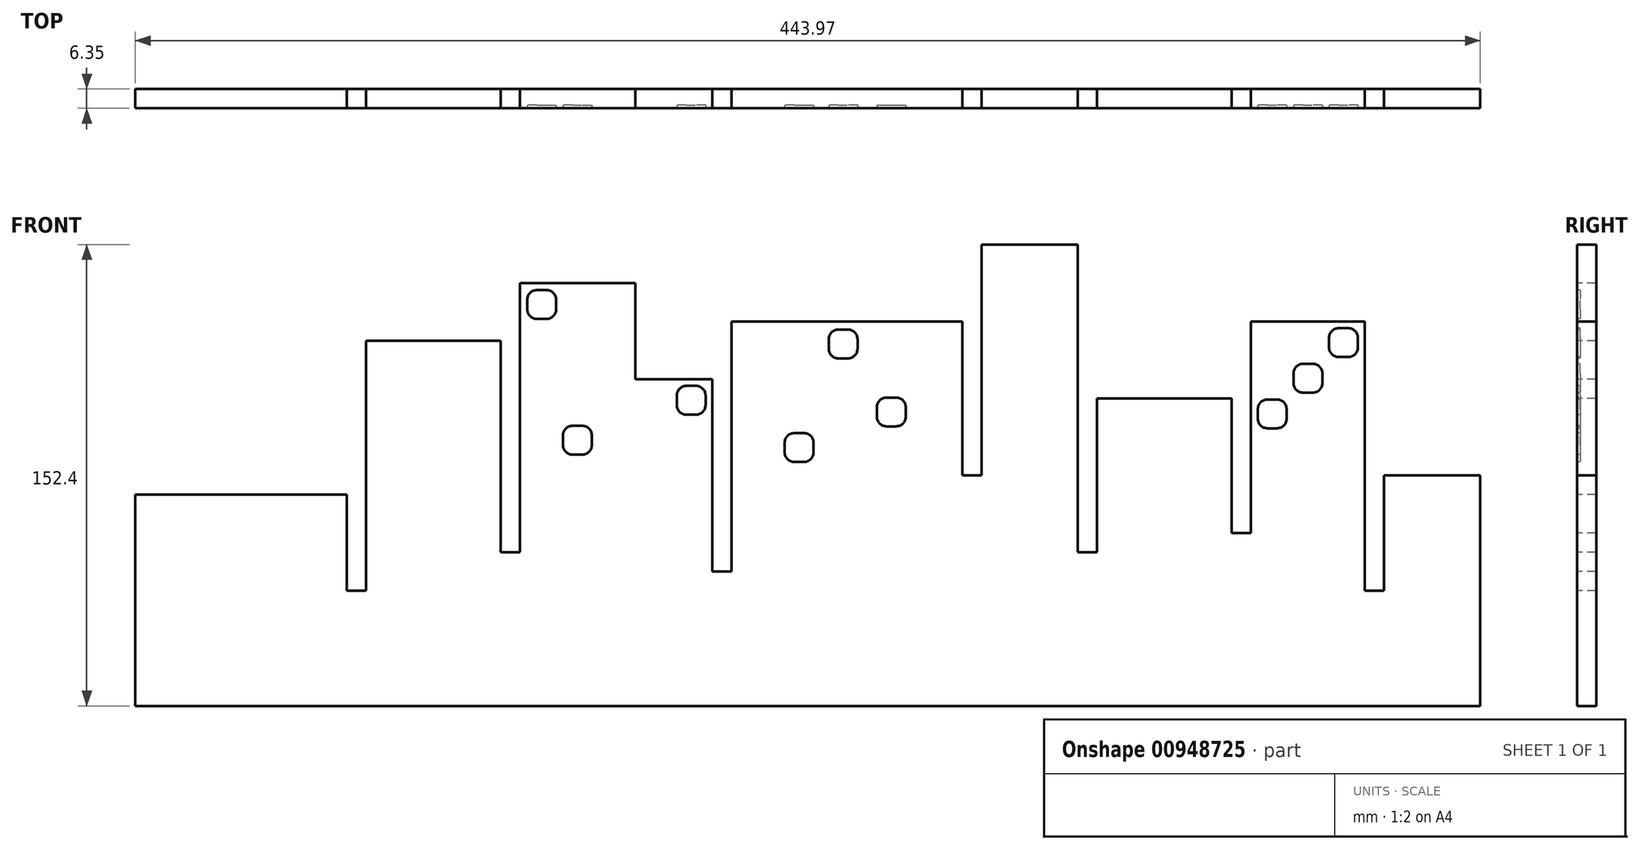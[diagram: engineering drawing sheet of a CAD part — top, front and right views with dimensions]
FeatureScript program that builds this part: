
annotation { "Feature Type Name" : "Feature", "Feature Type Description" : "" }
export const myFeature = defineFeature(function(context is Context, id is Id, definition is map)
    precondition{}
    {
        {
            var Q0;
            Q0=qCreatedBy(makeId("Front.planeOp"),FACE);
            var sketch = newSketch(context, id + "F0", { "sketchPlane" : qUnion([Q0])});
            skLineSegment(sketch, "E0.bottom", {"start": v(-28.68, 31.43) * mm, "end": v(-25.5, 31.43) * mm});
            skLineSegment(sketch, "E0.top", {"start": v(-28.68, 21.9) * mm, "end": v(-25.5, 21.9) * mm});
            skLineSegment(sketch, "E0.left", {"start": v(-31.86, 28.26) * mm, "end": v(-31.86, 25.08) * mm});
            skLineSegment(sketch, "E0.right", {"start": v(-22.33, 28.26) * mm, "end": v(-22.33, 25.08) * mm});
            skPoint(sketch, "E1.visualSharp", {"position": v(-31.86, 31.43) * mm});
            skArc(sketch, "E1.filletArc", {"start": v(-28.68, 31.43) * mm, "mid": v(-30.93, 30.5) * mm, "end": v(-31.86, 28.26) * mm});
            skPoint(sketch, "E2.visualSharp", {"position": v(-22.33, 31.43) * mm});
            skArc(sketch, "E2.filletArc", {"start": v(-22.33, 28.26) * mm, "mid": v(-23.26, 30.5) * mm, "end": v(-25.5, 31.43) * mm});
            skPoint(sketch, "E3.visualSharp", {"position": v(-22.33, 21.9) * mm});
            skArc(sketch, "E3.filletArc", {"start": v(-25.5, 21.9) * mm, "mid": v(-23.26, 22.84) * mm, "end": v(-22.33, 25.08) * mm});
            skPoint(sketch, "E4.visualSharp", {"position": v(-31.86, 21.9) * mm});
            skArc(sketch, "E4.filletArc", {"start": v(-31.86, 25.08) * mm, "mid": v(-30.93, 22.84) * mm, "end": v(-28.68, 21.9) * mm});
            skLineSegment(sketch, "E5", {"start": v(-22.33, 31.43) * mm, "end": v(-20.09, 33.68) * mm});
            skLineSegment(sketch, "E6.bottom", {"start": v(-16.91, 43.2) * mm, "end": v(-13.74, 43.2) * mm});
            skLineSegment(sketch, "E6.top", {"start": v(-16.91, 33.68) * mm, "end": v(-13.74, 33.68) * mm});
            skLineSegment(sketch, "E6.left", {"start": v(-20.09, 40.03) * mm, "end": v(-20.09, 36.85) * mm});
            skLineSegment(sketch, "E6.right", {"start": v(-10.56, 40.03) * mm, "end": v(-10.56, 36.85) * mm});
            skPoint(sketch, "E7.visualSharp", {"position": v(-20.09, 43.2) * mm});
            skArc(sketch, "E7.filletArc", {"start": v(-16.91, 43.2) * mm, "mid": v(-19.16, 42.27) * mm, "end": v(-20.09, 40.03) * mm});
            skPoint(sketch, "E8.visualSharp", {"position": v(-10.56, 43.2) * mm});
            skArc(sketch, "E8.filletArc", {"start": v(-10.56, 40.03) * mm, "mid": v(-11.5, 42.27) * mm, "end": v(-13.74, 43.2) * mm});
            skPoint(sketch, "E9.visualSharp", {"position": v(-10.56, 33.68) * mm});
            skArc(sketch, "E9.filletArc", {"start": v(-13.74, 33.68) * mm, "mid": v(-11.5, 34.6) * mm, "end": v(-10.56, 36.85) * mm});
            skPoint(sketch, "E10.visualSharp", {"position": v(-20.09, 33.68) * mm});
            skArc(sketch, "E10.filletArc", {"start": v(-20.09, 36.85) * mm, "mid": v(-19.16, 34.6) * mm, "end": v(-16.91, 33.68) * mm});
            skLineSegment(sketch, "E11", {"start": v(-10.56, 43.2) * mm, "end": v(-8.32, 45.45) * mm});
            skLineSegment(sketch, "E12.bottom", {"start": v(-5.14, 54.97) * mm, "end": v(-1.97, 54.97) * mm});
            skLineSegment(sketch, "E12.top", {"start": v(-5.14, 45.45) * mm, "end": v(-1.97, 45.45) * mm});
            skLineSegment(sketch, "E12.left", {"start": v(-8.32, 51.8) * mm, "end": v(-8.32, 48.62) * mm});
            skLineSegment(sketch, "E12.right", {"start": v(1.2, 51.8) * mm, "end": v(1.2, 48.62) * mm});
            skPoint(sketch, "E13.visualSharp", {"position": v(-8.32, 54.97) * mm});
            skArc(sketch, "E13.filletArc", {"start": v(-5.14, 54.97) * mm, "mid": v(-7.39, 54.04) * mm, "end": v(-8.32, 51.8) * mm});
            skPoint(sketch, "E14.visualSharp", {"position": v(1.2, 54.97) * mm});
            skArc(sketch, "E14.filletArc", {"start": v(1.2, 51.8) * mm, "mid": v(0.28, 54.04) * mm, "end": v(-1.97, 54.97) * mm});
            skPoint(sketch, "E15.visualSharp", {"position": v(1.2, 45.45) * mm});
            skArc(sketch, "E15.filletArc", {"start": v(-1.97, 45.45) * mm, "mid": v(0.28, 46.38) * mm, "end": v(1.2, 48.62) * mm});
            skPoint(sketch, "E16.visualSharp", {"position": v(-8.32, 45.45) * mm});
            skArc(sketch, "E16.filletArc", {"start": v(-8.32, 48.62) * mm, "mid": v(-7.39, 46.38) * mm, "end": v(-5.14, 45.45) * mm});
            skPoint(sketch, "E17.visualSharp", {"position": v(-20.9, 30.05) * mm});
            skLineSegment(sketch, "E18", {"start": v(-20.9, 30.05) * mm, "end": v(-18.65, 32.3) * mm});
            skPoint(sketch, "E19.visualSharp", {"position": v(-18.65, 32.3) * mm});
            skPoint(sketch, "E20.visualSharp", {"position": v(-34.1, 19.66) * mm});
            skLineSegment(sketch, "E21", {"start": v(-34.1, 19.66) * mm, "end": v(-31.86, 21.9) * mm});
            skLineSegment(sketch, "E22", {"start": v(1.2, 54.97) * mm, "end": v(3.47, 57.2) * mm});
            skPoint(sketch, "E23.visualSharp", {"position": v(3.47, 57.2) * mm});
            skLineSegment(sketch, "E24.bottom", {"start": v(3.47, 57.2) * mm, "end": v(-34.1, 57.2) * mm});
            skLineSegment(sketch, "E24.left", {"start": v(3.47, 57.2) * mm, "end": v(3.47, -31.7) * mm});
            skLineSegment(sketch, "E24.right", {"start": v(-34.1, 57.2) * mm, "end": v(-34.1, -12.64) * mm});
            skLineSegment(sketch, "E25.right", {"start": v(3.47, 19.66) * mm, "end": v(3.47, 19.65) * mm});
            skLineSegment(sketch, "E26.top", {"start": v(-34.1, -69.8) * mm, "end": v(3.47, -69.8) * mm});
            skLineSegment(sketch, "E27.bottom", {"start": v(9.82, -69.8) * mm, "end": v(41.57, -69.8) * mm});
            skLineSegment(sketch, "E27.top", {"start": v(9.82, 6.4) * mm, "end": v(41.57, 6.4) * mm});
            skLineSegment(sketch, "E27.left", {"start": v(9.82, -31.7) * mm, "end": v(9.82, 6.4) * mm});
            skLineSegment(sketch, "E27.right", {"start": v(41.57, -69.8) * mm, "end": v(41.57, 6.4) * mm});
            skLineSegment(sketch, "E28.bottom", {"start": v(-34.1, -69.8) * mm, "end": v(-40.45, -69.8) * mm});
            skLineSegment(sketch, "E28.top", {"start": v(-34.1, -12.64) * mm, "end": v(-40.45, -12.64) * mm});
            skLineSegment(sketch, "E29.bottom", {"start": v(-40.45, -69.8) * mm, "end": v(-84.9, -69.8) * mm});
            skLineSegment(sketch, "E29.top", {"start": v(-40.45, 31.8) * mm, "end": v(-84.9, 31.8) * mm});
            skLineSegment(sketch, "E29.left", {"start": v(-40.45, -12.64) * mm, "end": v(-40.45, 31.8) * mm});
            skLineSegment(sketch, "E29.right", {"start": v(-84.9, -19) * mm, "end": v(-84.9, 31.8) * mm});
            skLineSegment(sketch, "E30.bottom", {"start": v(-84.9, -69.8) * mm, "end": v(-91.25, -69.8) * mm});
            skLineSegment(sketch, "E30.top", {"start": v(-84.9, -19) * mm, "end": v(-91.25, -19) * mm});
            skLineSegment(sketch, "E31.bottom", {"start": v(-91.25, -69.8) * mm, "end": v(-123, -69.8) * mm});
            skLineSegment(sketch, "E31.top", {"start": v(-91.25, 82.6) * mm, "end": v(-123, 82.6) * mm});
            skLineSegment(sketch, "E31.left", {"start": v(-91.25, -19) * mm, "end": v(-91.25, 82.6) * mm});
            skLineSegment(sketch, "E31.right", {"start": v(-123, 6.4) * mm, "end": v(-123, 82.6) * mm});
            skLineSegment(sketch, "E32.bottom", {"start": v(-123, -69.8) * mm, "end": v(-129.35, -69.8) * mm});
            skLineSegment(sketch, "E32.top", {"start": v(-123, 6.4) * mm, "end": v(-129.35, 6.4) * mm});
            skLineSegment(sketch, "E33.bottom", {"start": v(-129.35, -69.8) * mm, "end": v(-205.55, -69.8) * mm});
            skLineSegment(sketch, "E33.top", {"start": v(-129.35, 57.2) * mm, "end": v(-205.55, 57.2) * mm});
            skLineSegment(sketch, "E33.left", {"start": v(-129.35, 6.4) * mm, "end": v(-129.35, 57.2) * mm});
            skLineSegment(sketch, "E33.right", {"start": v(-205.55, -25.34) * mm, "end": v(-205.55, 57.2) * mm});
            skLineSegment(sketch, "E34.bottom", {"start": v(-205.55, -69.8) * mm, "end": v(-211.9, -69.8) * mm});
            skLineSegment(sketch, "E34.top", {"start": v(-205.55, -25.34) * mm, "end": v(-211.9, -25.34) * mm});
            skLineSegment(sketch, "E35.bottom", {"start": v(-211.9, -69.8) * mm, "end": v(-237.3, -69.8) * mm});
            skLineSegment(sketch, "E35.top", {"start": v(-211.9, 38.16) * mm, "end": v(-237.3, 38.16) * mm});
            skLineSegment(sketch, "E35.left", {"start": v(-211.9, -25.34) * mm, "end": v(-211.9, 38.16) * mm});
            skLineSegment(sketch, "E36.bottom", {"start": v(-237.3, -69.8) * mm, "end": v(-275.4, -69.8) * mm});
            skLineSegment(sketch, "E36.top", {"start": v(-237.3, 69.9) * mm, "end": v(-275.4, 69.9) * mm});
            skLineSegment(sketch, "E36.left", {"start": v(-237.3, 38.16) * mm, "end": v(-237.3, 69.9) * mm});
            skLineSegment(sketch, "E36.right", {"start": v(-275.4, -19) * mm, "end": v(-275.4, 69.9) * mm});
            skLineSegment(sketch, "E37.bottom", {"start": v(-275.4, -69.8) * mm, "end": v(-281.75, -69.8) * mm});
            skLineSegment(sketch, "E37.top", {"start": v(-275.4, -19) * mm, "end": v(-281.75, -19) * mm});
            skLineSegment(sketch, "E38.bottom", {"start": v(-281.75, -69.8) * mm, "end": v(-326.2, -69.8) * mm});
            skLineSegment(sketch, "E38.top", {"start": v(-281.75, 50.86) * mm, "end": v(-326.2, 50.86) * mm});
            skLineSegment(sketch, "E38.left", {"start": v(-281.75, -19) * mm, "end": v(-281.75, 50.86) * mm});
            skLineSegment(sketch, "E38.right", {"start": v(-326.2, -31.7) * mm, "end": v(-326.2, 50.86) * mm});
            skLineSegment(sketch, "E39.bottom", {"start": v(-326.2, -69.8) * mm, "end": v(-332.55, -69.8) * mm});
            skLineSegment(sketch, "E39.top", {"start": v(-326.2, -31.7) * mm, "end": v(-332.55, -31.7) * mm});
            skLineSegment(sketch, "E40.bottom", {"start": v(-332.55, -69.8) * mm, "end": v(-402.4, -69.8) * mm});
            skLineSegment(sketch, "E40.top", {"start": v(-332.55, 0.06) * mm, "end": v(-402.4, 0.06) * mm});
            skLineSegment(sketch, "E40.left", {"start": v(-332.55, -31.7) * mm, "end": v(-332.55, 0.06) * mm});
            skLineSegment(sketch, "E40.right", {"start": v(-402.4, -69.8) * mm, "end": v(-402.4, 0.06) * mm});
            skLineSegment(sketch, "E41.bottom", {"start": v(-184.85, 20.32) * mm, "end": v(-181.67, 20.32) * mm});
            skLineSegment(sketch, "E41.top", {"start": v(-184.85, 10.8) * mm, "end": v(-181.67, 10.8) * mm});
            skLineSegment(sketch, "E41.left", {"start": v(-188.02, 17.14) * mm, "end": v(-188.02, 13.97) * mm});
            skLineSegment(sketch, "E41.right", {"start": v(-178.5, 17.14) * mm, "end": v(-178.5, 13.97) * mm});
            skPoint(sketch, "E42.visualSharp", {"position": v(-188.02, 20.32) * mm});
            skArc(sketch, "E42.filletArc", {"start": v(-184.85, 20.32) * mm, "mid": v(-187.1, 19.4) * mm, "end": v(-188.02, 17.14) * mm});
            skPoint(sketch, "E43.visualSharp", {"position": v(-190.27, 42.76) * mm});
            skArc(sketch, "E43.filletArc", {"start": v(-178.5, 17.14) * mm, "mid": v(-179.43, 19.4) * mm, "end": v(-181.67, 20.32) * mm});
            skPoint(sketch, "E44.visualSharp", {"position": v(-178.5, 10.8) * mm});
            skArc(sketch, "E44.filletArc", {"start": v(-181.67, 10.8) * mm, "mid": v(-179.43, 11.72) * mm, "end": v(-178.5, 13.97) * mm});
            skPoint(sketch, "E45.visualSharp", {"position": v(-188.02, 10.8) * mm});
            skArc(sketch, "E45.filletArc", {"start": v(-188.02, 13.97) * mm, "mid": v(-187.1, 11.72) * mm, "end": v(-184.85, 10.8) * mm});
            skLineSegment(sketch, "E46", {"start": v(-84.9, 17.75) * mm, "end": v(-82.66, 20) * mm});
            skLineSegment(sketch, "E47.bottom", {"start": v(-170.34, 54.53) * mm, "end": v(-167.17, 54.53) * mm});
            skLineSegment(sketch, "E47.top", {"start": v(-170.34, 45) * mm, "end": v(-167.17, 45) * mm});
            skLineSegment(sketch, "E47.left", {"start": v(-173.52, 51.35) * mm, "end": v(-173.52, 48.18) * mm});
            skLineSegment(sketch, "E47.right", {"start": v(-164, 51.35) * mm, "end": v(-164, 48.18) * mm});
            skPoint(sketch, "E48.visualSharp", {"position": v(-173.52, 54.53) * mm});
            skArc(sketch, "E48.filletArc", {"start": v(-170.34, 54.53) * mm, "mid": v(-172.59, 53.6) * mm, "end": v(-173.52, 51.35) * mm});
            skPoint(sketch, "E49.visualSharp", {"position": v(-164, 54.53) * mm});
            skArc(sketch, "E49.filletArc", {"start": v(-164, 51.35) * mm, "mid": v(-164.92, 53.6) * mm, "end": v(-167.17, 54.53) * mm});
            skPoint(sketch, "E50.visualSharp", {"position": v(-164, 45) * mm});
            skArc(sketch, "E50.filletArc", {"start": v(-167.17, 45) * mm, "mid": v(-164.92, 45.93) * mm, "end": v(-164, 48.18) * mm});
            skPoint(sketch, "E51.visualSharp", {"position": v(-173.52, 45) * mm});
            skArc(sketch, "E51.filletArc", {"start": v(-173.52, 48.18) * mm, "mid": v(-172.59, 45.93) * mm, "end": v(-170.34, 45) * mm});
            skLineSegment(sketch, "E52", {"start": v(-73.13, 29.52) * mm, "end": v(-70.89, 31.77) * mm});
            skLineSegment(sketch, "E53.bottom", {"start": v(-154.43, 32.08) * mm, "end": v(-151.25, 32.08) * mm});
            skLineSegment(sketch, "E53.top", {"start": v(-154.43, 22.56) * mm, "end": v(-151.25, 22.56) * mm});
            skLineSegment(sketch, "E53.left", {"start": v(-157.6, 28.9) * mm, "end": v(-157.6, 25.73) * mm});
            skLineSegment(sketch, "E53.right", {"start": v(-148.08, 28.9) * mm, "end": v(-148.08, 25.73) * mm});
            skPoint(sketch, "E54.visualSharp", {"position": v(-157.6, 32.08) * mm});
            skArc(sketch, "E54.filletArc", {"start": v(-154.43, 32.08) * mm, "mid": v(-156.67, 31.15) * mm, "end": v(-157.6, 28.9) * mm});
            skPoint(sketch, "E55.visualSharp", {"position": v(-148.08, 32.08) * mm});
            skArc(sketch, "E55.filletArc", {"start": v(-148.08, 28.9) * mm, "mid": v(-149, 31.15) * mm, "end": v(-151.25, 32.08) * mm});
            skPoint(sketch, "E56.visualSharp", {"position": v(-148.08, 22.56) * mm});
            skArc(sketch, "E56.filletArc", {"start": v(-151.25, 22.56) * mm, "mid": v(-149, 23.49) * mm, "end": v(-148.08, 25.73) * mm});
            skPoint(sketch, "E57.visualSharp", {"position": v(-176.25, 56.77) * mm});
            skArc(sketch, "E57.filletArc", {"start": v(-157.6, 25.73) * mm, "mid": v(-156.67, 23.49) * mm, "end": v(-154.43, 22.56) * mm});
            skPoint(sketch, "E58.visualSharp", {"position": v(-174.32, 41.38) * mm});
            skLineSegment(sketch, "E59", {"start": v(-188.83, 41.38) * mm, "end": v(-186.59, 43.62) * mm});
            skPoint(sketch, "E60.visualSharp", {"position": v(-172.08, 43.62) * mm});
            skPoint(sketch, "E61.visualSharp", {"position": v(-190.27, 8.55) * mm});
            skPoint(sketch, "E62.visualSharp", {"position": v(-40.45, 9.38) * mm});
            skLineSegment(sketch, "E63.bottom", {"start": v(-181.67, 20.32) * mm, "end": v(-148.08, 20.32) * mm});
            skLineSegment(sketch, "E63.top", {"start": v(-181.67, 22.56) * mm, "end": v(-148.08, 22.56) * mm});
            skLineSegment(sketch, "E63.left", {"start": v(-181.67, 20.32) * mm, "end": v(-181.67, 22.56) * mm});
            skLineSegment(sketch, "E63.right", {"start": v(-148.08, 20.32) * mm, "end": v(-148.08, 22.56) * mm});
            skLineSegment(sketch, "E64.bottom", {"start": v(-261.24, 16.38) * mm, "end": v(-261.24, 19.56) * mm});
            skLineSegment(sketch, "E64.top", {"start": v(-251.71, 16.38) * mm, "end": v(-251.71, 19.56) * mm});
            skLineSegment(sketch, "E64.left", {"start": v(-258.06, 13.2) * mm, "end": v(-254.89, 13.2) * mm});
            skLineSegment(sketch, "E64.right", {"start": v(-258.06, 22.73) * mm, "end": v(-254.89, 22.73) * mm});
            skPoint(sketch, "E65.visualSharp", {"position": v(-261.24, 13.2) * mm});
            skArc(sketch, "E65.filletArc", {"start": v(-261.24, 16.38) * mm, "mid": v(-260.3, 14.14) * mm, "end": v(-258.06, 13.2) * mm});
            skPoint(sketch, "E66.visualSharp", {"position": v(-261.24, 22.73) * mm});
            skArc(sketch, "E66.filletArc", {"start": v(-258.06, 22.73) * mm, "mid": v(-260.3, 21.8) * mm, "end": v(-261.24, 19.56) * mm});
            skPoint(sketch, "E67.visualSharp", {"position": v(-251.71, 22.73) * mm});
            skArc(sketch, "E67.filletArc", {"start": v(-251.71, 19.56) * mm, "mid": v(-252.64, 21.8) * mm, "end": v(-254.89, 22.73) * mm});
            skPoint(sketch, "E68.visualSharp", {"position": v(-251.71, 13.2) * mm});
            skArc(sketch, "E68.filletArc", {"start": v(-254.89, 13.2) * mm, "mid": v(-252.64, 14.14) * mm, "end": v(-251.71, 16.38) * mm});
            skLineSegment(sketch, "E69", {"start": v(-261.24, 55.8) * mm, "end": v(-263.48, 58.04) * mm});
            skLineSegment(sketch, "E70.bottom", {"start": v(-273, 61.21) * mm, "end": v(-273, 64.39) * mm});
            skLineSegment(sketch, "E70.top", {"start": v(-263.48, 61.21) * mm, "end": v(-263.48, 64.39) * mm});
            skLineSegment(sketch, "E70.left", {"start": v(-269.83, 58.04) * mm, "end": v(-266.66, 58.04) * mm});
            skLineSegment(sketch, "E70.right", {"start": v(-269.83, 67.56) * mm, "end": v(-266.66, 67.56) * mm});
            skPoint(sketch, "E71.visualSharp", {"position": v(-273, 58.04) * mm});
            skArc(sketch, "E71.filletArc", {"start": v(-273, 61.21) * mm, "mid": v(-272.08, 58.97) * mm, "end": v(-269.83, 58.04) * mm});
            skPoint(sketch, "E72.visualSharp", {"position": v(-273, 67.56) * mm});
            skArc(sketch, "E72.filletArc", {"start": v(-269.83, 67.56) * mm, "mid": v(-272.08, 66.63) * mm, "end": v(-273, 64.39) * mm});
            skPoint(sketch, "E73.visualSharp", {"position": v(-263.48, 67.56) * mm});
            skArc(sketch, "E73.filletArc", {"start": v(-263.48, 64.39) * mm, "mid": v(-264.41, 66.63) * mm, "end": v(-266.66, 67.56) * mm});
            skPoint(sketch, "E74.visualSharp", {"position": v(-263.48, 58.04) * mm});
            skArc(sketch, "E74.filletArc", {"start": v(-266.66, 58.04) * mm, "mid": v(-264.41, 58.97) * mm, "end": v(-263.48, 61.21) * mm});
            skLineSegment(sketch, "E75", {"start": v(-273, 67.56) * mm, "end": v(-275.25, 69.8) * mm});
            skLineSegment(sketch, "E76.bottom", {"start": v(-220.5, 35.92) * mm, "end": v(-217.33, 35.92) * mm});
            skLineSegment(sketch, "E76.top", {"start": v(-220.5, 26.4) * mm, "end": v(-217.33, 26.4) * mm});
            skLineSegment(sketch, "E76.left", {"start": v(-223.68, 32.75) * mm, "end": v(-223.68, 29.57) * mm});
            skLineSegment(sketch, "E76.right", {"start": v(-214.16, 32.75) * mm, "end": v(-214.16, 29.57) * mm});
            skPoint(sketch, "E77.visualSharp", {"position": v(-223.68, 35.92) * mm});
            skArc(sketch, "E77.filletArc", {"start": v(-220.5, 35.92) * mm, "mid": v(-222.75, 35) * mm, "end": v(-223.68, 32.75) * mm});
            skPoint(sketch, "E78.visualSharp", {"position": v(-214.16, 35.92) * mm});
            skArc(sketch, "E78.filletArc", {"start": v(-214.16, 32.75) * mm, "mid": v(-215.09, 35) * mm, "end": v(-217.33, 35.92) * mm});
            skPoint(sketch, "E79.visualSharp", {"position": v(-214.16, 26.4) * mm});
            skArc(sketch, "E79.filletArc", {"start": v(-217.33, 26.4) * mm, "mid": v(-215.09, 27.33) * mm, "end": v(-214.16, 29.57) * mm});
            skPoint(sketch, "E80.visualSharp", {"position": v(-275.25, 69.8) * mm});
            skArc(sketch, "E80.filletArc", {"start": v(-223.68, 29.57) * mm, "mid": v(-222.75, 27.33) * mm, "end": v(-220.5, 26.4) * mm});
            skPoint(sketch, "E81.visualSharp", {"position": v(-259.86, 24.17) * mm});
            skLineSegment(sketch, "E82", {"start": v(-259.86, 24.17) * mm, "end": v(-262.1, 26.41) * mm});
            skPoint(sketch, "E83.visualSharp", {"position": v(-262.1, 26.41) * mm});
            skPoint(sketch, "E84.visualSharp", {"position": v(-249.47, 10.96) * mm});
            skPoint(sketch, "E85.visualSharp", {"position": v(-211.9, 38.16) * mm});
            skLineSegment(sketch, "E86.bottom", {"start": v(3.47, -69.8) * mm, "end": v(9.82, -69.8) * mm});
            skLineSegment(sketch, "E86.top", {"start": v(3.47, -31.7) * mm, "end": v(9.82, -31.7) * mm});
            skSolve(sketch);
        }
        {
            var Q0;
            Q0=makeQuery(id+"F0.imprint","IMPRINT",FACE,{"disambiguationData":[TD([[makeQuery(id+"F0.imprint","IMPRINT",EDGE,{"derivedFrom":sQuery(id+"F0.wireOp",EDGE,"E70.bottom")}),-1.0]])]});
            var Q1;
            Q1=makeQuery(id+"F0.imprint","IMPRINT",FACE,{"disambiguationData":[TD([[makeQuery(id+"F0.imprint","IMPRINT",EDGE,{"derivedFrom":sQuery(id+"F0.wireOp",EDGE,"E63.bottom")}),1.0]])]});
            var Q2;
            Q2=makeQuery(id+"F0.imprint","IMPRINT",FACE,{"disambiguationData":[TD([[makeQuery(id+"F0.imprint","IMPRINT",EDGE,{"derivedFrom":sQuery(id+"F0.wireOp",EDGE,"E0.bottom")}),1.0]])]});
            var Q3;
            Q3=makeQuery(id+"F0.imprint","IMPRINT",FACE,{"disambiguationData":[TD([[makeQuery(id+"F0.imprint","IMPRINT",EDGE,{"derivedFrom":sQuery(id+"F0.wireOp",EDGE,"E41.bottom")}),-1.0]])]});
            var Q4;
            Q4=makeQuery(id+"F0.imprint","IMPRINT",FACE,{"disambiguationData":[TD([[makeQuery(id+"F0.imprint","IMPRINT",EDGE,{"derivedFrom":sQuery(id+"F0.wireOp",EDGE,"E0.bottom")}),-1.0]])]});
            var Q5;
            Q5=makeQuery(id+"F0.imprint","IMPRINT",FACE,{"disambiguationData":[TD([[makeQuery(id+"F0.imprint","IMPRINT",EDGE,{"derivedFrom":sQuery(id+"F0.wireOp",EDGE,"E53.bottom")}),-1.0]])]});
            var Q6;
            Q6=makeQuery(id+"F0.imprint","IMPRINT",FACE,{"disambiguationData":[TD([[makeQuery(id+"F0.imprint","IMPRINT",EDGE,{"derivedFrom":sQuery(id+"F0.wireOp",EDGE,"E6.bottom")}),-1.0]])]});
            var Q7;
            Q7=makeQuery(id+"F0.imprint","IMPRINT",FACE,{"disambiguationData":[TD([[makeQuery(id+"F0.imprint","IMPRINT",EDGE,{"derivedFrom":sQuery(id+"F0.wireOp",EDGE,"E64.bottom")}),-1.0]])]});
            var Q8;
            Q8=makeQuery(id+"F0.imprint","IMPRINT",FACE,{"disambiguationData":[TD([[makeQuery(id+"F0.imprint","IMPRINT",EDGE,{"derivedFrom":sQuery(id+"F0.wireOp",EDGE,"E47.bottom")}),-1.0]])]});
            var Q9;
            Q9=makeQuery(id+"F0.imprint","IMPRINT",FACE,{"disambiguationData":[TD([[makeQuery(id+"F0.imprint","IMPRINT",EDGE,{"derivedFrom":sQuery(id+"F0.wireOp",EDGE,"E12.bottom")}),-1.0]])]});
            var Q10;
            Q10=makeQuery(id+"F0.imprint","IMPRINT",FACE,{"disambiguationData":[TD([[makeQuery(id+"F0.imprint","IMPRINT",EDGE,{"derivedFrom":sQuery(id+"F0.wireOp",EDGE,"E76.bottom")}),-1.0]])]});
            extrude(context, id + "F1", {"entities" : qUnion([Q0, Q1, Q2, Q3, Q4, Q5, Q6, Q7, Q8, Q9, Q10]), "oppositeDirection" : true, "depth" : 6.35 * mm, "offsetDistance" : 25.4 * mm});
        }
        {
            var Q0;
            Q0=makeQuery(id+"F0.imprint","IMPRINT",FACE,{"disambiguationData":[TD([[makeQuery(id+"F0.imprint","IMPRINT",EDGE,{"derivedFrom":sQuery(id+"F0.wireOp",EDGE,"E70.bottom")}),-1.0]])]});
            var Q1;
            Q1=makeQuery(id+"F0.imprint","IMPRINT",FACE,{"disambiguationData":[TD([[makeQuery(id+"F0.imprint","IMPRINT",EDGE,{"derivedFrom":sQuery(id+"F0.wireOp",EDGE,"E64.bottom")}),-1.0]])]});
            var Q2;
            Q2=makeQuery(id+"F0.imprint","IMPRINT",FACE,{"disambiguationData":[TD([[makeQuery(id+"F0.imprint","IMPRINT",EDGE,{"derivedFrom":sQuery(id+"F0.wireOp",EDGE,"E76.bottom")}),-1.0]])]});
            var Q3;
            Q3=makeQuery(id+"F0.imprint","IMPRINT",FACE,{"disambiguationData":[TD([[makeQuery(id+"F0.imprint","IMPRINT",EDGE,{"derivedFrom":sQuery(id+"F0.wireOp",EDGE,"E47.bottom")}),-1.0]])]});
            var Q4;
            Q4=makeQuery(id+"F0.imprint","IMPRINT",FACE,{"disambiguationData":[TD([[makeQuery(id+"F0.imprint","IMPRINT",EDGE,{"derivedFrom":sQuery(id+"F0.wireOp",EDGE,"E41.bottom")}),-1.0]])]});
            var Q5;
            Q5=makeQuery(id+"F0.imprint","IMPRINT",FACE,{"disambiguationData":[TD([[makeQuery(id+"F0.imprint","IMPRINT",EDGE,{"derivedFrom":sQuery(id+"F0.wireOp",EDGE,"E53.bottom")}),-1.0]])]});
            var Q6;
            Q6=makeQuery(id+"F0.imprint","IMPRINT",FACE,{"disambiguationData":[TD([[makeQuery(id+"F0.imprint","IMPRINT",EDGE,{"derivedFrom":sQuery(id+"F0.wireOp",EDGE,"E0.bottom")}),-1.0]])]});
            var Q7;
            Q7=makeQuery(id+"F0.imprint","IMPRINT",FACE,{"disambiguationData":[TD([[makeQuery(id+"F0.imprint","IMPRINT",EDGE,{"derivedFrom":sQuery(id+"F0.wireOp",EDGE,"E6.bottom")}),-1.0]])]});
            var Q8;
            Q8=makeQuery(id+"F0.imprint","IMPRINT",FACE,{"disambiguationData":[TD([[makeQuery(id+"F0.imprint","IMPRINT",EDGE,{"derivedFrom":sQuery(id+"F0.wireOp",EDGE,"E12.bottom")}),-1.0]])]});
            extrude(context, id + "F2", {"entities" : qUnion([Q0, Q1, Q2, Q3, Q4, Q5, Q6, Q7, Q8]), "operationType" : NewBodyOperationType.REMOVE, "oppositeDirection" : true, "depth" : 1.02 * mm, "offsetDistance" : 25.4 * mm});
        }
    });
